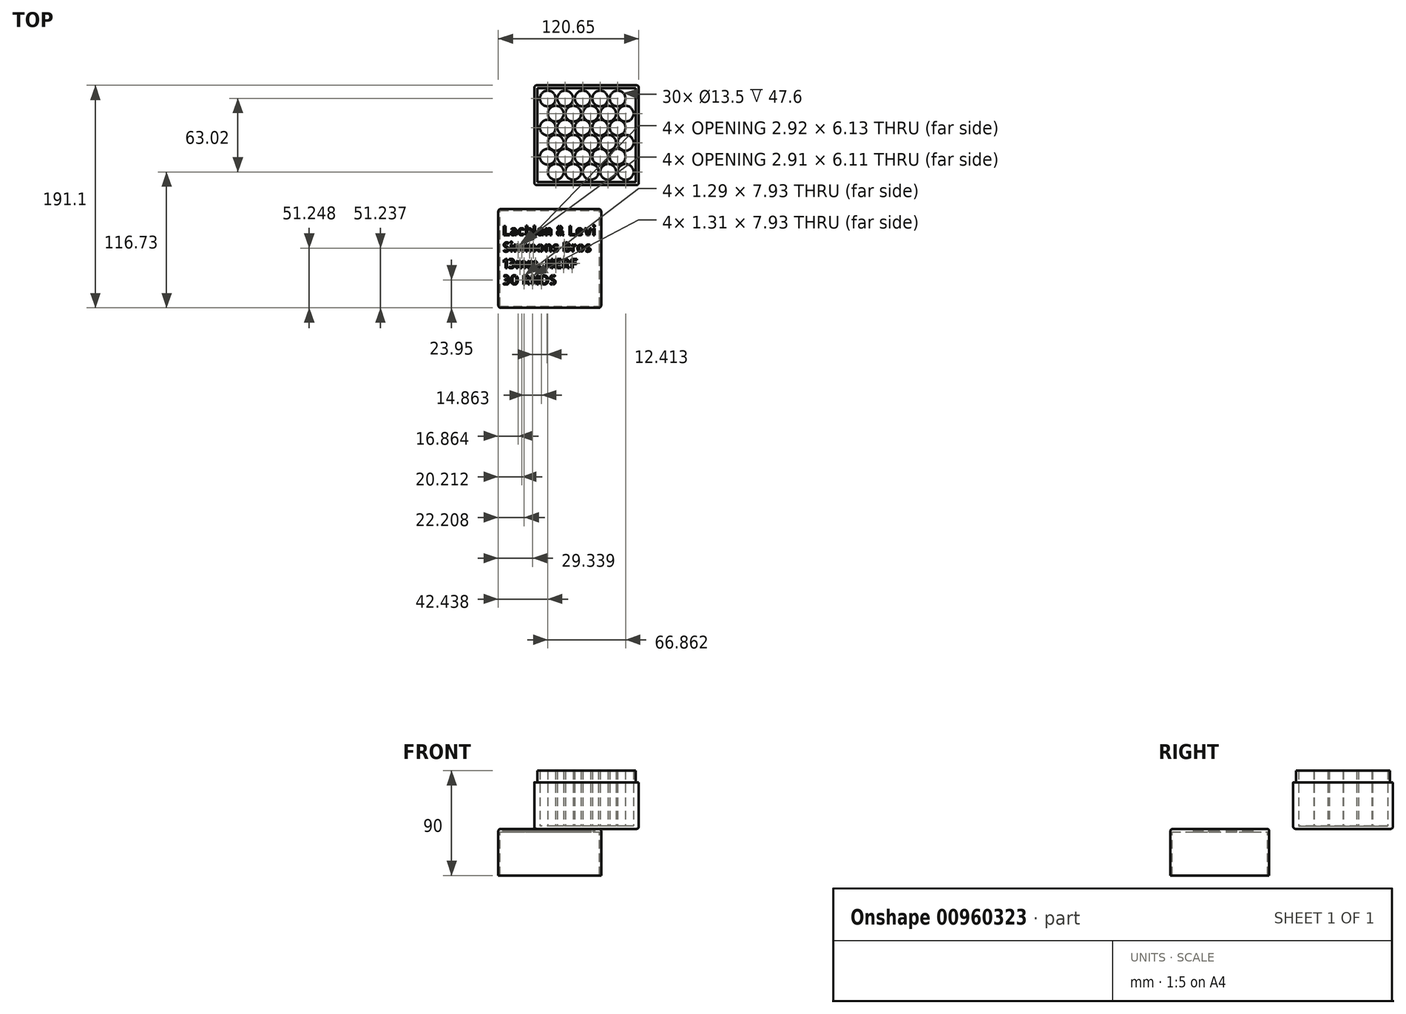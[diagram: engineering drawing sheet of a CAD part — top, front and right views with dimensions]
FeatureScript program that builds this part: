
annotation { "Feature Type Name" : "Feature", "Feature Type Description" : "" }
export const myFeature = defineFeature(function(context is Context, id is Id, definition is map)
    precondition{}
    {
        {
            var Q0;
            Q0=qCreatedBy(makeId("Top.planeOp"),FACE);
            var sketch = newSketch(context, id + "F0", { "sketchPlane" : qUnion([Q0])});
            skCircle(sketch, "E0", {"center": v(-44.46, 23.32) * mm, "radius": 6.75 * mm});
            skCircle(sketch, "E1.0.1.0", {"center": v(-37.6, 10.3) * mm, "radius": 6.75 * mm});
            skCircle(sketch, "E1.1.0.0", {"center": v(-29.46, 23.32) * mm, "radius": 6.75 * mm});
            skCircle(sketch, "E1.1.1.0", {"center": v(-22.6, 10.3) * mm, "radius": 6.75 * mm});
            skCircle(sketch, "E1.2.0.0", {"center": v(-14.46, 23.32) * mm, "radius": 6.75 * mm});
            skCircle(sketch, "E1.2.1.0", {"center": v(-7.6, 10.3) * mm, "radius": 6.75 * mm});
            skCircle(sketch, "E1.3.0.0", {"center": v(0.54, 23.32) * mm, "radius": 6.75 * mm});
            skCircle(sketch, "E1.3.1.0", {"center": v(7.4, 10.3) * mm, "radius": 6.75 * mm});
            skCircle(sketch, "E1.4.0.0", {"center": v(15.54, 23.32) * mm, "radius": 6.75 * mm});
            skCircle(sketch, "E1.4.1.0", {"center": v(22.4, 10.3) * mm, "radius": 6.75 * mm});
            skLineSegment(sketch, "E1.direction1", {"start": v(-44.46, 23.32) * mm, "end": v(-29.46, 23.32) * mm, "construction": true});
            skLineSegment(sketch, "E1.direction2", {"start": v(-44.46, 23.32) * mm, "end": v(-37.6, 10.3) * mm, "construction": true});
            skLineSegment(sketch, "E2.0.1.0", {"start": v(-44.46, -1.68) * mm, "end": v(-29.46, -1.68) * mm, "construction": true});
            skLineSegment(sketch, "E2.0.1.1", {"start": v(-44.46, -1.68) * mm, "end": v(-37.6, -14.7) * mm, "construction": true});
            skCircle(sketch, "E2.0.1.2", {"center": v(-44.46, -1.68) * mm, "radius": 6.75 * mm});
            skCircle(sketch, "E2.0.1.3", {"center": v(-37.6, -14.7) * mm, "radius": 6.75 * mm});
            skCircle(sketch, "E2.0.1.4", {"center": v(-29.46, -1.68) * mm, "radius": 6.75 * mm});
            skCircle(sketch, "E2.0.1.5", {"center": v(-22.6, -14.7) * mm, "radius": 6.75 * mm});
            skCircle(sketch, "E2.0.1.6", {"center": v(-14.46, -1.68) * mm, "radius": 6.75 * mm});
            skCircle(sketch, "E2.0.1.7", {"center": v(-7.6, -14.7) * mm, "radius": 6.75 * mm});
            skCircle(sketch, "E2.0.1.8", {"center": v(0.54, -1.68) * mm, "radius": 6.75 * mm});
            skCircle(sketch, "E2.0.1.9", {"center": v(7.4, -14.7) * mm, "radius": 6.75 * mm});
            skCircle(sketch, "E2.0.1.10", {"center": v(15.54, -1.68) * mm, "radius": 6.75 * mm});
            skCircle(sketch, "E2.0.1.11", {"center": v(22.4, -14.7) * mm, "radius": 6.75 * mm});
            skLineSegment(sketch, "E2.0.2.0", {"start": v(-44.46, -26.68) * mm, "end": v(-29.46, -26.68) * mm, "construction": true});
            skLineSegment(sketch, "E2.0.2.1", {"start": v(-44.46, -26.68) * mm, "end": v(-37.6, -39.7) * mm, "construction": true});
            skCircle(sketch, "E2.0.2.2", {"center": v(-44.46, -26.68) * mm, "radius": 6.75 * mm});
            skCircle(sketch, "E2.0.2.3", {"center": v(-37.6, -39.7) * mm, "radius": 6.75 * mm});
            skCircle(sketch, "E2.0.2.4", {"center": v(-29.46, -26.68) * mm, "radius": 6.75 * mm});
            skCircle(sketch, "E2.0.2.5", {"center": v(-22.6, -39.7) * mm, "radius": 6.75 * mm});
            skCircle(sketch, "E2.0.2.6", {"center": v(-14.46, -26.68) * mm, "radius": 6.75 * mm});
            skCircle(sketch, "E2.0.2.7", {"center": v(-7.6, -39.7) * mm, "radius": 6.75 * mm});
            skCircle(sketch, "E2.0.2.8", {"center": v(0.54, -26.68) * mm, "radius": 6.75 * mm});
            skCircle(sketch, "E2.0.2.9", {"center": v(7.4, -39.7) * mm, "radius": 6.75 * mm});
            skCircle(sketch, "E2.0.2.10", {"center": v(15.54, -26.68) * mm, "radius": 6.75 * mm});
            skCircle(sketch, "E2.0.2.11", {"center": v(22.4, -39.7) * mm, "radius": 6.75 * mm});
            skLineSegment(sketch, "E2.direction1", {"start": v(-37.6, 10.3) * mm, "end": v(-12.6, 10.3) * mm, "construction": true});
            skLineSegment(sketch, "E2.direction2", {"start": v(-37.6, 10.3) * mm, "end": v(-37.6, -14.7) * mm, "construction": true});
            skLineSegment(sketch, "E3.bottom", {"start": v(-53.35, 32.07) * mm, "end": v(31.15, 32.07) * mm});
            skLineSegment(sketch, "E3.top", {"start": v(-53.35, -48.45) * mm, "end": v(31.15, -48.45) * mm});
            skLineSegment(sketch, "E3.left", {"start": v(-53.35, 32.07) * mm, "end": v(-53.35, -48.45) * mm});
            skLineSegment(sketch, "E3.right", {"start": v(31.15, 32.07) * mm, "end": v(31.15, -48.45) * mm});
            skLineSegment(sketch, "E4.bottom", {"start": v(-85.5, -155.03) * mm, "end": v(0, -155.03) * mm});
            skLineSegment(sketch, "E4.top", {"start": v(-85.5, -73.03) * mm, "end": v(0, -73.03) * mm});
            skLineSegment(sketch, "E4.left", {"start": v(-85.5, -155.03) * mm, "end": v(-85.5, -73.03) * mm});
            skLineSegment(sketch, "E4.right", {"start": v(0, -155.03) * mm, "end": v(0, -73.03) * mm});
            skLineSegment(sketch, "E5.0", {"start": v(-86.9, -156.43) * mm, "end": v(1.4, -156.43) * mm});
            skLineSegment(sketch, "E5.1", {"start": v(-86.9, -156.43) * mm, "end": v(-86.9, -71.63) * mm});
            skLineSegment(sketch, "E5.2", {"start": v(-86.9, -71.63) * mm, "end": v(1.4, -71.63) * mm});
            skLineSegment(sketch, "E5.3", {"start": v(1.4, -156.43) * mm, "end": v(1.4, -71.63) * mm});
            skLineSegment(sketch, "E6.0", {"start": v(-55.95, 34.67) * mm, "end": v(-55.95, -51.05) * mm});
            skLineSegment(sketch, "E6.1", {"start": v(-55.95, 34.67) * mm, "end": v(33.75, 34.67) * mm});
            skLineSegment(sketch, "E6.2", {"start": v(33.75, 34.67) * mm, "end": v(33.75, -51.05) * mm});
            skLineSegment(sketch, "E6.3", {"start": v(-55.95, -51.05) * mm, "end": v(33.75, -51.05) * mm});
            skText(sketch, "E7", { "text": "Lachlan & Levi\nSimmons Bros\n13mm, NERF\n30 RNDS", "fontName": "AllertaStencil-Regular.ttf"});
            const initialGuessF0  = {"E7": [-0.08313, -0.09415, 1, 0, 0.00793]};
            skSetInitialGuess(sketch, initialGuessF0);
            skSolve(sketch);
        }
        {
            var Q0;
            Q0=makeQuery(id+"F0.imprint","IMPRINT",FACE,{"disambiguationData":[TD([[makeQuery(id+"F0.imprint","IMPRINT",EDGE,{"derivedFrom":sQuery(id+"F0.wireOp",EDGE,"E0")}),-1.0]])]});
            extrude(context, id + "F1", {"entities" : qUnion([Q0]), "depth" : 50 * mm, "offsetDistance" : 25 * mm});
        }
        {
            var Q0;
            Q0=makeQuery(id+"F0.imprint","IMPRINT",FACE,{"disambiguationData":[TD([[makeQuery(id+"F0.imprint","IMPRINT",EDGE,{"derivedFrom":sQuery(id+"F0.wireOp",EDGE,"E2.0.2.3")}),1.0]])]});
            var Q1;
            Q1=makeQuery(id+"F0.imprint","IMPRINT",FACE,{"disambiguationData":[TD([[makeQuery(id+"F0.imprint","IMPRINT",EDGE,{"derivedFrom":sQuery(id+"F0.wireOp",EDGE,"E2.0.2.5")}),1.0]])]});
            var Q2;
            Q2=makeQuery(id+"F0.imprint","IMPRINT",FACE,{"disambiguationData":[TD([[makeQuery(id+"F0.imprint","IMPRINT",EDGE,{"derivedFrom":sQuery(id+"F0.wireOp",EDGE,"E2.0.2.7")}),1.0]])]});
            var Q3;
            Q3=makeQuery(id+"F0.imprint","IMPRINT",FACE,{"disambiguationData":[TD([[makeQuery(id+"F0.imprint","IMPRINT",EDGE,{"derivedFrom":sQuery(id+"F0.wireOp",EDGE,"E2.0.2.9")}),1.0]])]});
            var Q4;
            Q4=makeQuery(id+"F0.imprint","IMPRINT",FACE,{"disambiguationData":[TD([[makeQuery(id+"F0.imprint","IMPRINT",EDGE,{"derivedFrom":sQuery(id+"F0.wireOp",EDGE,"E2.0.2.11")}),1.0]])]});
            var Q5;
            Q5=makeQuery(id+"F0.imprint","IMPRINT",FACE,{"disambiguationData":[TD([[makeQuery(id+"F0.imprint","IMPRINT",EDGE,{"derivedFrom":sQuery(id+"F0.wireOp",EDGE,"E2.0.2.2")}),1.0]])]});
            var Q6;
            Q6=makeQuery(id+"F0.imprint","IMPRINT",FACE,{"disambiguationData":[TD([[makeQuery(id+"F0.imprint","IMPRINT",EDGE,{"derivedFrom":sQuery(id+"F0.wireOp",EDGE,"E2.0.2.4")}),1.0]])]});
            var Q7;
            Q7=makeQuery(id+"F0.imprint","IMPRINT",FACE,{"disambiguationData":[TD([[makeQuery(id+"F0.imprint","IMPRINT",EDGE,{"derivedFrom":sQuery(id+"F0.wireOp",EDGE,"E2.0.2.6")}),1.0]])]});
            var Q8;
            Q8=makeQuery(id+"F0.imprint","IMPRINT",FACE,{"disambiguationData":[TD([[makeQuery(id+"F0.imprint","IMPRINT",EDGE,{"derivedFrom":sQuery(id+"F0.wireOp",EDGE,"E2.0.2.8")}),1.0]])]});
            var Q9;
            Q9=makeQuery(id+"F0.imprint","IMPRINT",FACE,{"disambiguationData":[TD([[makeQuery(id+"F0.imprint","IMPRINT",EDGE,{"derivedFrom":sQuery(id+"F0.wireOp",EDGE,"E2.0.2.10")}),1.0]])]});
            var Q10;
            Q10=makeQuery(id+"F0.imprint","IMPRINT",FACE,{"disambiguationData":[TD([[makeQuery(id+"F0.imprint","IMPRINT",EDGE,{"derivedFrom":sQuery(id+"F0.wireOp",EDGE,"E2.0.1.3")}),1.0]])]});
            var Q11;
            Q11=makeQuery(id+"F0.imprint","IMPRINT",FACE,{"disambiguationData":[TD([[makeQuery(id+"F0.imprint","IMPRINT",EDGE,{"derivedFrom":sQuery(id+"F0.wireOp",EDGE,"E2.0.1.5")}),1.0]])]});
            var Q12;
            Q12=makeQuery(id+"F0.imprint","IMPRINT",FACE,{"disambiguationData":[TD([[makeQuery(id+"F0.imprint","IMPRINT",EDGE,{"derivedFrom":sQuery(id+"F0.wireOp",EDGE,"E2.0.1.7")}),1.0]])]});
            var Q13;
            Q13=makeQuery(id+"F0.imprint","IMPRINT",FACE,{"disambiguationData":[TD([[makeQuery(id+"F0.imprint","IMPRINT",EDGE,{"derivedFrom":sQuery(id+"F0.wireOp",EDGE,"E2.0.1.9")}),1.0]])]});
            var Q14;
            Q14=makeQuery(id+"F0.imprint","IMPRINT",FACE,{"disambiguationData":[TD([[makeQuery(id+"F0.imprint","IMPRINT",EDGE,{"derivedFrom":sQuery(id+"F0.wireOp",EDGE,"E2.0.1.11")}),1.0]])]});
            var Q15;
            Q15=makeQuery(id+"F0.imprint","IMPRINT",FACE,{"disambiguationData":[TD([[makeQuery(id+"F0.imprint","IMPRINT",EDGE,{"derivedFrom":sQuery(id+"F0.wireOp",EDGE,"E2.0.1.2")}),1.0]])]});
            var Q16;
            Q16=makeQuery(id+"F0.imprint","IMPRINT",FACE,{"disambiguationData":[TD([[makeQuery(id+"F0.imprint","IMPRINT",EDGE,{"derivedFrom":sQuery(id+"F0.wireOp",EDGE,"E2.0.1.4")}),1.0]])]});
            var Q17;
            Q17=makeQuery(id+"F0.imprint","IMPRINT",FACE,{"disambiguationData":[TD([[makeQuery(id+"F0.imprint","IMPRINT",EDGE,{"derivedFrom":sQuery(id+"F0.wireOp",EDGE,"E2.0.1.6")}),1.0]])]});
            var Q18;
            Q18=makeQuery(id+"F0.imprint","IMPRINT",FACE,{"disambiguationData":[TD([[makeQuery(id+"F0.imprint","IMPRINT",EDGE,{"derivedFrom":sQuery(id+"F0.wireOp",EDGE,"E2.0.1.8")}),1.0]])]});
            var Q19;
            Q19=makeQuery(id+"F0.imprint","IMPRINT",FACE,{"disambiguationData":[TD([[makeQuery(id+"F0.imprint","IMPRINT",EDGE,{"derivedFrom":sQuery(id+"F0.wireOp",EDGE,"E2.0.1.10")}),1.0]])]});
            var Q20;
            Q20=makeQuery(id+"F0.imprint","IMPRINT",FACE,{"disambiguationData":[TD([[makeQuery(id+"F0.imprint","IMPRINT",EDGE,{"derivedFrom":sQuery(id+"F0.wireOp",EDGE,"E1.0.1.0")}),1.0]])]});
            var Q21;
            Q21=makeQuery(id+"F0.imprint","IMPRINT",FACE,{"disambiguationData":[TD([[makeQuery(id+"F0.imprint","IMPRINT",EDGE,{"derivedFrom":sQuery(id+"F0.wireOp",EDGE,"E1.1.1.0")}),1.0]])]});
            var Q22;
            Q22=makeQuery(id+"F0.imprint","IMPRINT",FACE,{"disambiguationData":[TD([[makeQuery(id+"F0.imprint","IMPRINT",EDGE,{"derivedFrom":sQuery(id+"F0.wireOp",EDGE,"E1.2.1.0")}),1.0]])]});
            var Q23;
            Q23=makeQuery(id+"F0.imprint","IMPRINT",FACE,{"disambiguationData":[TD([[makeQuery(id+"F0.imprint","IMPRINT",EDGE,{"derivedFrom":sQuery(id+"F0.wireOp",EDGE,"E1.3.1.0")}),1.0]])]});
            var Q24;
            Q24=makeQuery(id+"F0.imprint","IMPRINT",FACE,{"disambiguationData":[TD([[makeQuery(id+"F0.imprint","IMPRINT",EDGE,{"derivedFrom":sQuery(id+"F0.wireOp",EDGE,"E1.4.1.0")}),1.0]])]});
            var Q25;
            Q25=makeQuery(id+"F0.imprint","IMPRINT",FACE,{"disambiguationData":[TD([[makeQuery(id+"F0.imprint","IMPRINT",EDGE,{"derivedFrom":sQuery(id+"F0.wireOp",EDGE,"E0")}),1.0]])]});
            var Q26;
            Q26=makeQuery(id+"F0.imprint","IMPRINT",FACE,{"disambiguationData":[TD([[makeQuery(id+"F0.imprint","IMPRINT",EDGE,{"derivedFrom":sQuery(id+"F0.wireOp",EDGE,"E1.1.0.0")}),1.0]])]});
            var Q27;
            Q27=makeQuery(id+"F0.imprint","IMPRINT",FACE,{"disambiguationData":[TD([[makeQuery(id+"F0.imprint","IMPRINT",EDGE,{"derivedFrom":sQuery(id+"F0.wireOp",EDGE,"E1.2.0.0")}),1.0]])]});
            var Q28;
            Q28=makeQuery(id+"F0.imprint","IMPRINT",FACE,{"disambiguationData":[TD([[makeQuery(id+"F0.imprint","IMPRINT",EDGE,{"derivedFrom":sQuery(id+"F0.wireOp",EDGE,"E1.3.0.0")}),1.0]])]});
            var Q29;
            Q29=makeQuery(id+"F0.imprint","IMPRINT",FACE,{"disambiguationData":[TD([[makeQuery(id+"F0.imprint","IMPRINT",EDGE,{"derivedFrom":sQuery(id+"F0.wireOp",EDGE,"E1.4.0.0")}),1.0]])]});
            extrude(context, id + "F2", {"entities" : qUnion([Q0, Q1, Q2, Q3, Q4, Q5, Q6, Q7, Q8, Q9, Q10, Q11, Q12, Q13, Q14, Q15, Q16, Q17, Q18, Q19, Q20, Q21, Q22, Q23, Q24, Q25, Q26, Q27, Q28, Q29]), "operationType" : NewBodyOperationType.ADD, "depth" : 2.4 * mm, "offsetDistance" : 25 * mm});
        }
        {
            var Q0;
            Q0=makeQuery(id+"F0.imprint","IMPRINT",FACE,{"disambiguationData":[TD([[makeQuery(id+"F0.imprint","IMPRINT",EDGE,{"derivedFrom":sQuery(id+"F0.wireOp",EDGE,"E4.bottom")}),1.0]])]});
            extrude(context, id + "F3", {"entities" : qUnion([Q0]), "oppositeDirection" : true, "depth" : 2.5 * mm, "offsetDistance" : 25 * mm});
        }
        {
            var Q0;
            Q0=makeQuery(id+"F0.imprint","IMPRINT",FACE,{"disambiguationData":[TD([[makeQuery(id+"F0.imprint","IMPRINT",EDGE,{"derivedFrom":sQuery(id+"F0.wireOp",EDGE,"E4.bottom")}),-1.0]])]});
            extrude(context, id + "F4", {"entities" : qUnion([Q0]), "operationType" : NewBodyOperationType.ADD, "oppositeDirection" : true, "depth" : 40 * mm, "offsetDistance" : 25 * mm});
        }
        {
            var Q0;
            Q0=makeQuery(id+"F0.imprint","IMPRINT",FACE,{"disambiguationData":[TD([[makeQuery(id+"F0.imprint","IMPRINT",EDGE,{"derivedFrom":sQuery(id+"F0.wireOp",EDGE,"E3.bottom")}),1.0]])]});
            extrude(context, id + "F5", {"entities" : qUnion([Q0]), "operationType" : NewBodyOperationType.ADD, "depth" : 40 * mm, "offsetDistance" : 25 * mm});
        }
        {
            var Q0;
            Q0=makeQuery(id+"F4.opExtrude","CAP_EDGE",EDGE,{"disambiguationData":[OSD([sQuery(id+"F0.wireOp",EDGE,"E5.0")])],"isStart":true});
            var Q1;
            Q1=makeQuery(id+"F4.opExtrude","CAP_EDGE",EDGE,{"disambiguationData":[OSD([sQuery(id+"F0.wireOp",EDGE,"E5.1")])],"isStart":true});
            var Q2;
            Q2=makeQuery(id+"F4.opExtrude","CAP_EDGE",EDGE,{"disambiguationData":[OSD([sQuery(id+"F0.wireOp",EDGE,"E5.2")])],"isStart":true});
            var Q3;
            Q3=makeQuery(id+"F4.opExtrude","SWEPT_EDGE",EDGE,{"disambiguationData":[OSD([sQuery(id+"F0.wireOp",EDGE,"E5.1"),sQuery(id+"F0.wireOp",EDGE,"E5.2")])]});
            var Q4;
            Q4=makeQuery(id+"F4.opExtrude","SWEPT_EDGE",EDGE,{"disambiguationData":[OSD([sQuery(id+"F0.wireOp",EDGE,"E5.2"),sQuery(id+"F0.wireOp",EDGE,"E5.3")])]});
            var Q5;
            Q5=makeQuery(id+"F4.opExtrude","CAP_EDGE",EDGE,{"disambiguationData":[OSD([sQuery(id+"F0.wireOp",EDGE,"E5.3")])],"isStart":true});
            var Q6;
            Q6=makeQuery(id+"F4.opExtrude","SWEPT_EDGE",EDGE,{"disambiguationData":[OSD([sQuery(id+"F0.wireOp",EDGE,"E5.0"),sQuery(id+"F0.wireOp",EDGE,"E5.1")])]});
            var Q7;
            Q7=makeQuery(id+"F4.opExtrude","SWEPT_EDGE",EDGE,{"disambiguationData":[OSD([sQuery(id+"F0.wireOp",EDGE,"E5.0"),sQuery(id+"F0.wireOp",EDGE,"E5.3")])]});
            fillet(context, id + "F6", {"entities" : qUnion([Q0, Q1, Q2, Q3, Q4, Q5, Q6, Q7]), "tangentPropagation" : true, "radius" : 2 * mm, "defaultsChanged" : false, "vertexSettings" : [], "allowEdgeOverflow" : false});
        }
        {
            var Q0;
            Q0=makeQuery(id+"F5.opExtrude","CAP_EDGE",EDGE,{"disambiguationData":[OSD([sQuery(id+"F0.wireOp",EDGE,"E6.1")])],"isStart":true});
            var Q1;
            Q1=makeQuery(id+"F5.opExtrude","CAP_EDGE",EDGE,{"disambiguationData":[OSD([sQuery(id+"F0.wireOp",EDGE,"E6.2")])],"isStart":true});
            var Q2;
            Q2=makeQuery(id+"F5.opExtrude","SWEPT_EDGE",EDGE,{"disambiguationData":[OSD([sQuery(id+"F0.wireOp",EDGE,"E6.1"),sQuery(id+"F0.wireOp",EDGE,"E6.2")])]});
            var Q3;
            Q3=makeQuery(id+"F5.opExtrude","SWEPT_EDGE",EDGE,{"disambiguationData":[OSD([sQuery(id+"F0.wireOp",EDGE,"E6.2"),sQuery(id+"F0.wireOp",EDGE,"E6.3")])]});
            var Q4;
            Q4=makeQuery(id+"F5.opExtrude","CAP_EDGE",EDGE,{"disambiguationData":[OSD([sQuery(id+"F0.wireOp",EDGE,"E6.3")])],"isStart":true});
            var Q5;
            Q5=makeQuery(id+"F5.opExtrude","CAP_EDGE",EDGE,{"disambiguationData":[OSD([sQuery(id+"F0.wireOp",EDGE,"E6.0")])],"isStart":true});
            var Q6;
            Q6=makeQuery(id+"F5.opExtrude","SWEPT_EDGE",EDGE,{"disambiguationData":[OSD([sQuery(id+"F0.wireOp",EDGE,"E6.0"),sQuery(id+"F0.wireOp",EDGE,"E6.1")])]});
            var Q7;
            Q7=makeQuery(id+"F5.opExtrude","SWEPT_EDGE",EDGE,{"disambiguationData":[OSD([sQuery(id+"F0.wireOp",EDGE,"E6.0"),sQuery(id+"F0.wireOp",EDGE,"E6.3")])]});
            fillet(context, id + "F7", {"entities" : qUnion([Q0, Q1, Q2, Q3, Q4, Q5, Q6, Q7]), "tangentPropagation" : true, "radius" : 2 * mm, "defaultsChanged" : true, "vertexSettings" : [], "allowEdgeOverflow" : false});
        }
    });
